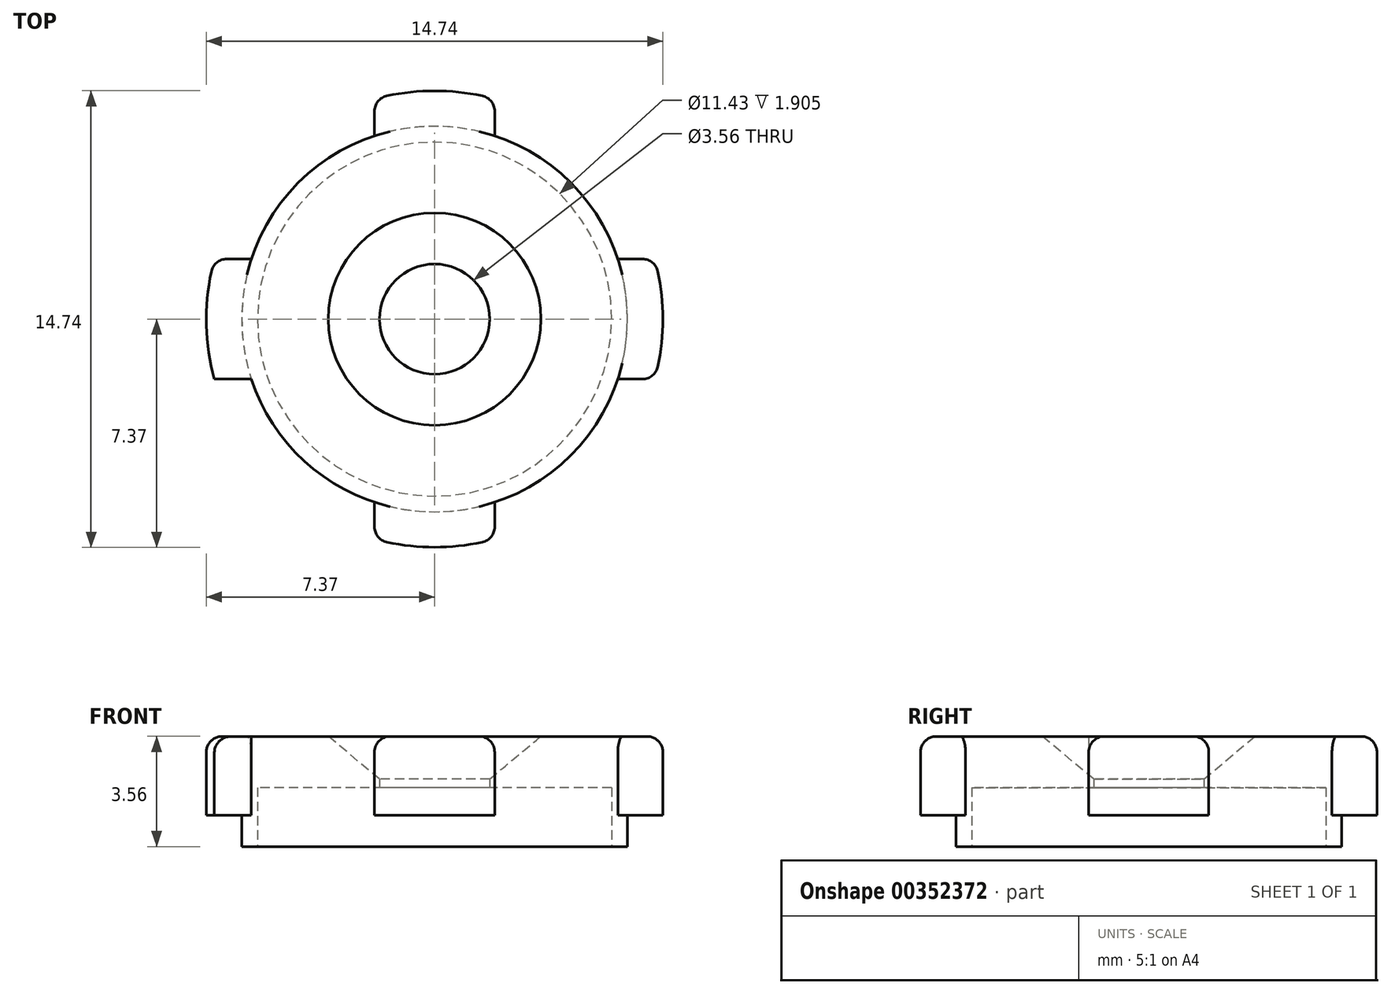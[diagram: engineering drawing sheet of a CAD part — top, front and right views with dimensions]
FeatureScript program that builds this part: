
annotation { "Feature Type Name" : "Feature", "Feature Type Description" : "" }
export const myFeature = defineFeature(function(context is Context, id is Id, definition is map)
    precondition{}
    {
        {
            var Q0;
            Q0=qCreatedBy(makeId("Top.planeOp"),FACE);
            var sketch = newSketch(context, id + "F0", { "sketchPlane" : qUnion([Q0])});
            skCircle(sketch, "E0", {"center": v(0, 0) * mm, "radius": 6.22 * mm});
            skCircle(sketch, "E1", {"center": v(0, 0) * mm, "radius": 5.71 * mm});
            skSolve(sketch);
        }
        {
            var Q0;
            Q0=makeQuery(id+"F0.imprint","IMPRINT",FACE,{"disambiguationData":[TD([[makeQuery(id+"F0.imprint","IMPRINT",EDGE,{"derivedFrom":sQuery(id+"F0.wireOp",EDGE,"E0")}),1.0]])]});
            extrude(context, id + "F1", {"entities" : qUnion([Q0]), "depth" : 1.02 * mm});
        }
        {
            var Q0;
            Q0=makeQuery(id+"F1.opExtrude","CAP_FACE",FACE,{"disambiguationData":[OSD([sQuery(id+"F0.wireOp",EDGE,"E0"),sQuery(id+"F0.wireOp",EDGE,"E1")])],"isStart":false});
            var sketch = newSketch(context, id + "F2", { "sketchPlane" : qUnion([Q0])});
            skCircle(sketch, "E2", {"center": v(0, 0) * mm, "radius": 1.78 * mm});
            skLineSegment(sketch, "E3", {"start": v(0, 0) * mm, "end": v(0, 9.32) * mm, "construction": true});
            skLineSegment(sketch, "E4", {"start": v(0, 0) * mm, "end": v(-6.64, 6.64) * mm, "construction": true});
            skLineSegment(sketch, "E5.MirrorCS", {"start": v(0, 0) * mm, "end": v(0, -9.32) * mm, "construction": true});
            skArc(sketch, "E6", {"start": v(-7.37, 0) * mm, "mid": v(-7.3, -0.98) * mm, "end": v(-7.1, -1.94) * mm});
            skLineSegment(sketch, "E7", {"start": v(-7.1, -1.94) * mm, "end": v(-5.91, -1.94) * mm});
            skArc(sketch, "E8.MirrorCS", {"start": v(-7.37, 0) * mm, "mid": v(-7.3, 0.98) * mm, "end": v(-7.1, 1.94) * mm});
            skLineSegment(sketch, "E9.MirrorCS", {"start": v(-7.1, 1.94) * mm, "end": v(-5.91, 1.94) * mm});
            skLineSegment(sketch, "E10.MirrorCS", {"start": v(7.1, -1.94) * mm, "end": v(5.91, -1.94) * mm});
            skArc(sketch, "E11.MirrorCS", {"start": v(7.37, 0) * mm, "mid": v(7.3, -0.98) * mm, "end": v(7.1, -1.94) * mm});
            skArc(sketch, "E12.MirrorCS", {"start": v(7.37, 0) * mm, "mid": v(7.3, 0.98) * mm, "end": v(7.1, 1.94) * mm});
            skLineSegment(sketch, "E13.MirrorCS", {"start": v(7.1, 1.94) * mm, "end": v(5.91, 1.94) * mm});
            skLineSegment(sketch, "E14.MirrorCS", {"start": v(-1.94, 7.1) * mm, "end": v(-1.94, 5.91) * mm});
            skArc(sketch, "E15.MirrorCS", {"start": v(0, 7.37) * mm, "mid": v(-0.98, 7.3) * mm, "end": v(-1.94, 7.1) * mm});
            skArc(sketch, "E16.MirrorCS", {"start": v(0, 7.37) * mm, "mid": v(0.98, 7.3) * mm, "end": v(1.94, 7.1) * mm});
            skLineSegment(sketch, "E17.MirrorCS", {"start": v(1.94, 7.1) * mm, "end": v(1.94, 5.91) * mm});
            skLineSegment(sketch, "E18.MirrorCS", {"start": v(-1.94, -7.1) * mm, "end": v(-1.94, -5.91) * mm});
            skArc(sketch, "E19.MirrorCS", {"start": v(0, -7.37) * mm, "mid": v(-0.98, -7.3) * mm, "end": v(-1.94, -7.1) * mm});
            skArc(sketch, "E20.MirrorCS", {"start": v(0, -7.37) * mm, "mid": v(0.98, -7.3) * mm, "end": v(1.94, -7.1) * mm});
            skLineSegment(sketch, "E21.MirrorCS", {"start": v(1.94, -7.1) * mm, "end": v(1.94, -5.91) * mm});
            skArc(sketch, "E22", {"start": v(-5.91, -1.94) * mm, "mid": v(-4.4, -4.4) * mm, "end": v(-1.94, -5.91) * mm});
            skArc(sketch, "E23.MirrorCS", {"start": v(-5.91, 1.94) * mm, "mid": v(-4.4, 4.4) * mm, "end": v(-1.94, 5.91) * mm});
            skArc(sketch, "E24.MirrorCS", {"start": v(5.91, 1.94) * mm, "mid": v(4.4, 4.4) * mm, "end": v(1.94, 5.91) * mm});
            skArc(sketch, "E25.MirrorCS", {"start": v(5.91, -1.94) * mm, "mid": v(4.4, -4.4) * mm, "end": v(1.94, -5.91) * mm});
            skSolve(sketch);
        }
        {
            var Q0;
            Q0=makeQuery(id+"F2.imprint","IMPRINT",FACE,{"disambiguationData":[TD([[makeQuery(id+"F2.imprint","IMPRINT",EDGE,{"derivedFrom":sQuery(id+"F2.wireOp",EDGE,"c5343c38-fbe1-466d-b0c2-a8c76e394a950.MirrorCS")}),-1.0]])]});
            var Q1;
            Q1=makeQuery(id+"F2.imprint","IMPRINT",FACE,{"disambiguationData":[TD([[makeQuery(id+"F2.imprint","IMPRINT",EDGE,{"derivedFrom":sQuery(id+"F2.wireOp",EDGE,"7d3f9132-a50a-406e-95e9-70e62c8006c82.MirrorCS")}),1.0]])]});
            var Q2;
            Q2=makeQuery(id+"F2.imprint","IMPRINT",FACE,{"disambiguationData":[TD([[makeQuery(id+"F2.imprint","IMPRINT",EDGE,{"derivedFrom":sQuery(id+"F2.wireOp",EDGE,"e8ndxUQa-desX-Tiex-mcuY-GLy8TxT6uqVA")}),-1.0]])]});
            var Q3;
            Q3=makeQuery(id+"F2.imprint","IMPRINT",FACE,{"disambiguationData":[TD([[makeQuery(id+"F2.imprint","IMPRINT",EDGE,{"derivedFrom":sQuery(id+"F2.wireOp",EDGE,"c4ce18c7-16a0-48e1-9e48-00f2b2494ce80.MirrorCS")}),-1.0]])]});
            var Q4;
            {var subQ2=sQuery(id+"F2.wireOp",EDGE,"6sWd79Q9-hn4f-APPS-rqXK-0ibGKo4Kr6yg");Q4=makeQuery(id+"F2.imprint","IMPRINT",FACE,{"disambiguationData":[TD([[makeQuery(id+"F2.imprint","IMPRINT",EDGE,{"derivedFrom":subQ2}),1.0]])]});}
            var Q5;
            Q5=makeQuery(id+"F2.imprint","IMPRINT",FACE,{"disambiguationData":[TD([[makeQuery(id+"F2.imprint","IMPRINT",EDGE,{"derivedFrom":sQuery(id+"F2.wireOp",EDGE,"E2")}),-1.0]])]});
            var Q6;
            {var subQ3=sQuery(id+"F2.wireOp",EDGE,"E22");Q6=makeQuery(id+"F2.imprint","IMPRINT",FACE,{"disambiguationData":[TD([[makeQuery(id+"F2.imprint","IMPRINT",EDGE,{"derivedFrom":subQ3}),1.0]])]});}
            var Q7;
            {var subQ1=sQuery(id+"F2.wireOp",EDGE,"E18.MirrorCS");Q7=makeQuery(id+"F2.imprint","IMPRINT",FACE,{"disambiguationData":[TD([[makeQuery(id+"F2.imprint","IMPRINT",EDGE,{"derivedFrom":subQ1}),-1.0]])]});}
            var Q8;
            {var subQ1=sQuery(id+"F2.wireOp",EDGE,"E10.MirrorCS");Q8=makeQuery(id+"F2.imprint","IMPRINT",FACE,{"disambiguationData":[TD([[makeQuery(id+"F2.imprint","IMPRINT",EDGE,{"derivedFrom":subQ1}),-1.0]])]});}
            var Q9;
            Q9=makeQuery(id+"F2.imprint","IMPRINT",FACE,{"disambiguationData":[TD([[makeQuery(id+"F2.imprint","IMPRINT",EDGE,{"derivedFrom":sQuery(id+"F2.wireOp",EDGE,"E6")}),1.0]])]});
            var Q10;
            {var subQ1=sQuery(id+"F2.wireOp",EDGE,"E14.MirrorCS");Q10=makeQuery(id+"F2.imprint","IMPRINT",FACE,{"disambiguationData":[TD([[makeQuery(id+"F2.imprint","IMPRINT",EDGE,{"derivedFrom":subQ1}),1.0]])]});}
            extrude(context, id + "F3", {"entities" : qUnion([Q0, Q1, Q2, Q3, Q4, Q5, Q6, Q7, Q8, Q9, Q10]), "operationType" : NewBodyOperationType.ADD, "depth" : 2.54 * mm});
        }
        {
            var Q0;
            Q0=qCreatedBy(makeId("Right.planeOp"),FACE);
            var sketch = newSketch(context, id + "F4", { "sketchPlane" : qUnion([Q0])});
            skLineSegment(sketch, "E26", {"start": v(0, 3.56) * mm, "end": v(-3.43, 3.56) * mm});
            skLineSegment(sketch, "E27", {"start": v(-3.43, 3.56) * mm, "end": v(0, 0.7) * mm});
            skLineSegment(sketch, "E28", {"start": v(0, -0.95) * mm, "end": v(0, 3.56) * mm, "construction": true});
            skLineSegment(sketch, "E29", {"start": v(0, 3.56) * mm, "end": v(0, 0.7) * mm});
            skSolve(sketch);
        }
        {
            var Q0;
            Q0 = qSketchRegion(id + "F4", true);
            var Q1;
            Q1=sQuery(id+"F4.wireOp",EDGE,"E28");
            revolve(context, id + "F5", {"operationType" : NewBodyOperationType.REMOVE, "entities" : qUnion([Q0]), "axis" : qUnion([Q1]), "revolveType" : RevolveType.ONE_DIRECTION, "oppositeDirection" : true, "angle" : 360 * degree});
        }
        {
            var Q0;
            Q0=makeQuery(id+"F0.imprint","IMPRINT",FACE,{"disambiguationData":[TD([[makeQuery(id+"F0.imprint","IMPRINT",EDGE,{"derivedFrom":sQuery(id+"F0.wireOp",EDGE,"E1")}),1.0]])]});
            extrude(context, id + "F6", {"entities" : qUnion([Q0]), "operationType" : NewBodyOperationType.REMOVE, "oppositeDirection" : true, "depth" : -1.9 * mm});
        }
        {
            var Q0;
            Q0=makeQuery(id+"F3.opExtrude","CAP_EDGE",EDGE,{"disambiguationData":[OSD([sQuery(id+"F2.wireOp",EDGE,"E19.MirrorCS"),sQuery(id+"F2.wireOp",EDGE,"E20.MirrorCS")])],"isStart":false});
            var Q1;
            Q1=makeQuery(id+"F3.opExtrude","CAP_EDGE",EDGE,{"disambiguationData":[OSD([sQuery(id+"F2.wireOp",EDGE,"E6"),sQuery(id+"F2.wireOp",EDGE,"E8.MirrorCS")])],"isStart":false});
            var Q2;
            Q2=makeQuery(id+"F3.opExtrude","CAP_EDGE",EDGE,{"disambiguationData":[OSD([sQuery(id+"F2.wireOp",EDGE,"E15.MirrorCS"),sQuery(id+"F2.wireOp",EDGE,"E16.MirrorCS")])],"isStart":false});
            var Q3;
            Q3=makeQuery(id+"F3.opExtrude","CAP_EDGE",EDGE,{"disambiguationData":[OSD([sQuery(id+"F2.wireOp",EDGE,"E11.MirrorCS"),sQuery(id+"F2.wireOp",EDGE,"E12.MirrorCS")])],"isStart":false});
            fillet(context, id + "F7", {"entities" : qUnion([Q0, Q1, Q2, Q3]), "radius" : 0.5 * mm, "tangentPropagation" : true, "allowEdgeOverflow" : false});
        }
        {
            var Q0;
            Q0=makeQuery(id+"F3.opExtrude","SWEPT_EDGE",EDGE,{"disambiguationData":[OSD([sQuery(id+"F2.wireOp",EDGE,"E20.MirrorCS"),sQuery(id+"F2.wireOp",EDGE,"E21.MirrorCS")])]});
            var Q1;
            Q1=makeQuery(id+"F3.opExtrude","SWEPT_EDGE",EDGE,{"disambiguationData":[OSD([sQuery(id+"F2.wireOp",EDGE,"E10.MirrorCS"),sQuery(id+"F2.wireOp",EDGE,"E11.MirrorCS")])]});
            var Q2;
            Q2=makeQuery(id+"F3.opExtrude","SWEPT_EDGE",EDGE,{"disambiguationData":[OSD([sQuery(id+"F2.wireOp",EDGE,"E12.MirrorCS"),sQuery(id+"F2.wireOp",EDGE,"E13.MirrorCS")])]});
            var Q3;
            Q3=makeQuery(id+"F3.opExtrude","SWEPT_EDGE",EDGE,{"disambiguationData":[OSD([sQuery(id+"F2.wireOp",EDGE,"E16.MirrorCS"),sQuery(id+"F2.wireOp",EDGE,"E17.MirrorCS")])]});
            var Q4;
            Q4=makeQuery(id+"F3.opExtrude","SWEPT_EDGE",EDGE,{"disambiguationData":[OSD([sQuery(id+"F2.wireOp",EDGE,"E14.MirrorCS"),sQuery(id+"F2.wireOp",EDGE,"E15.MirrorCS")])]});
            var Q5;
            Q5=makeQuery(id+"F3.opExtrude","SWEPT_EDGE",EDGE,{"disambiguationData":[OSD([sQuery(id+"F2.wireOp",EDGE,"E8.MirrorCS"),sQuery(id+"F2.wireOp",EDGE,"E9.MirrorCS")])]});
            var Q6;
            Q6=makeQuery(id+"F3.opExtrude","SWEPT_EDGE",EDGE,{"disambiguationData":[OSD([sQuery(id+"F2.wireOp",EDGE,"E18.MirrorCS"),sQuery(id+"F2.wireOp",EDGE,"E19.MirrorCS")])]});
            fillet(context, id + "F8", {"entities" : qUnion([Q0, Q1, Q2, Q3, Q4, Q5, Q6]), "radius" : 0.5 * mm, "tangentPropagation" : true, "allowEdgeOverflow" : false});
        }
    });
